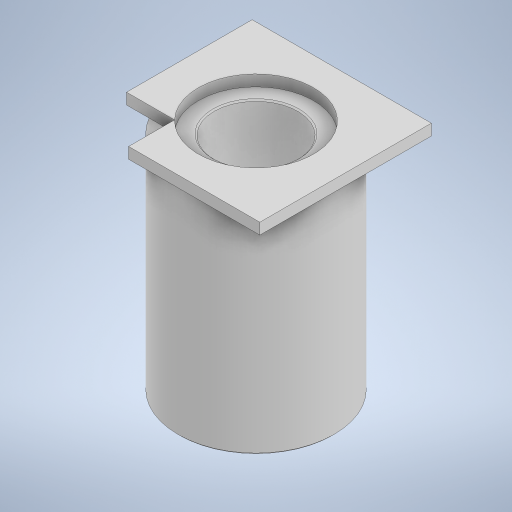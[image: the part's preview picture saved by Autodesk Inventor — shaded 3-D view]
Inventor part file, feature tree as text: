
AUTODESK INVENTOR PART (.ipt)
format: ipt  version: 2024 (Build 280153000, 153)  size: 249,344 bytes
history: native  units: in
note: dims shown in document units (in); Inventor stores cm internally (conversion verified against a paired STEP export)
features: extrude x2, chamfer x1, sketch x1
ambient origin geometry x8: Origin, YZ Plane, XZ Plane, XY Plane, X Axis, Y Axis, Z Axis, Center Point
bodies: Solid1 (feature_tree)
feature tree (4):
  extrude  "Extrusion1"  Depth=0.1in
  chamfer  "Chamfer1"  Distance=2.0in
  extrude  "Extrusion2"  Depth=0.1in TaperAngle=45.0deg
  sketch  "Sketch3"  dims[d0=1.4in d1=0.75in d2=2.0in d3=0.0in d4=0.0125in d5=0.125in d6=45.0deg d7=0.1in d8=0.0in]
